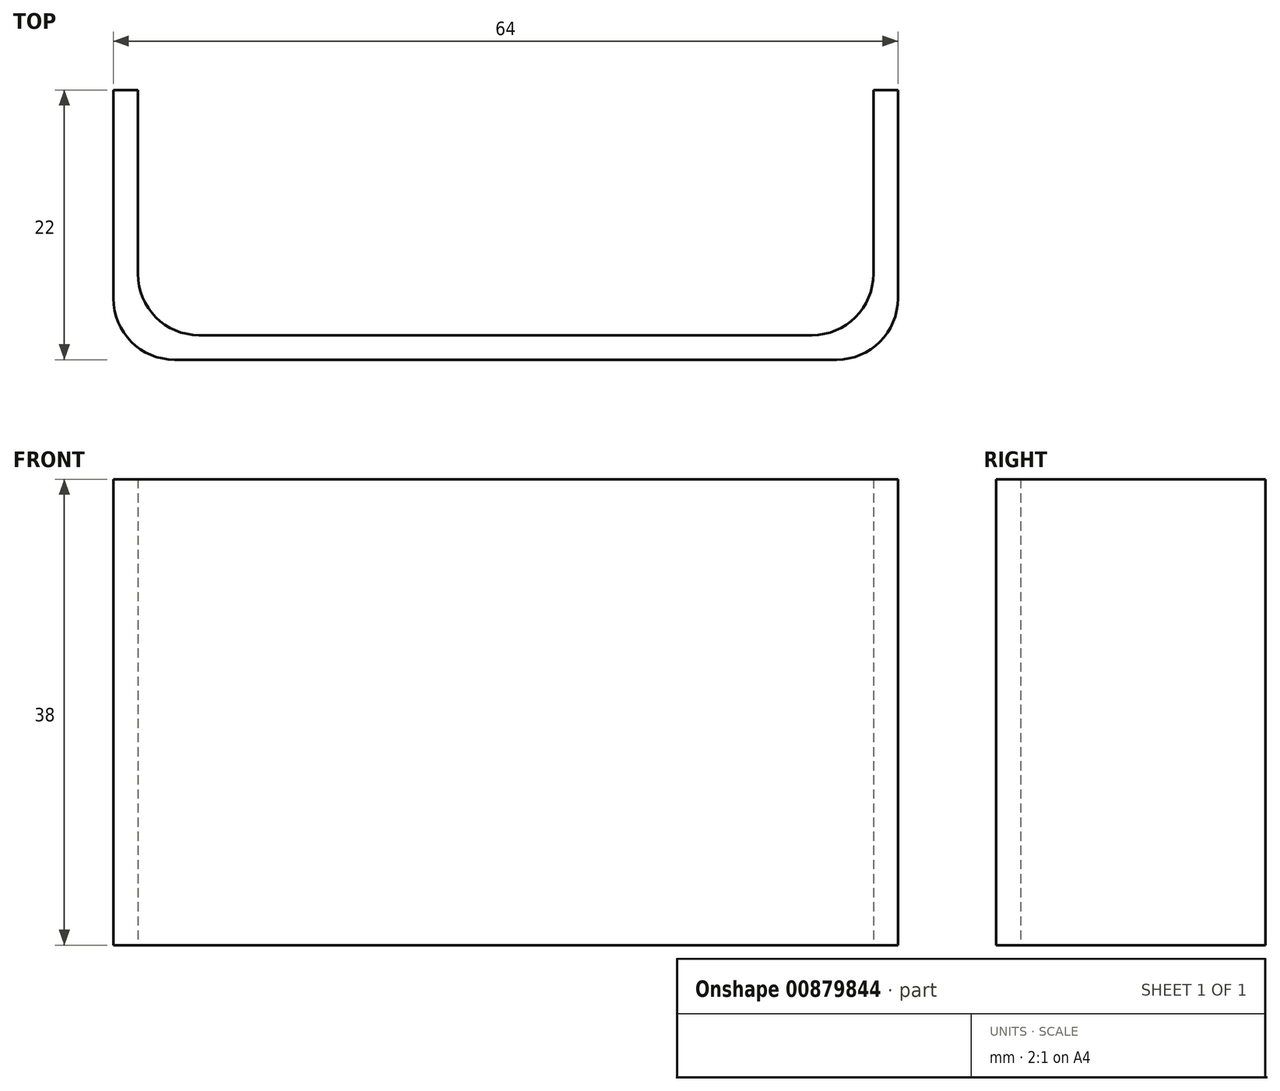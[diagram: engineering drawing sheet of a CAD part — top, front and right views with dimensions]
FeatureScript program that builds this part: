
annotation { "Feature Type Name" : "Feature", "Feature Type Description" : "" }
export const myFeature = defineFeature(function(context is Context, id is Id, definition is map)
    precondition{}
    {
        {
            var Q0;
            Q0=qCreatedBy(makeId("Top.planeOp"),FACE);
            var sketch = newSketch(context, id + "F0", { "sketchPlane" : qUnion([Q0])});
            skLineSegment(sketch, "E0", {"start": v(0, 0) * mm, "end": v(25, 0) * mm});
            skLineSegment(sketch, "E1", {"start": v(30, 5) * mm, "end": v(30, 20) * mm});
            skLineSegment(sketch, "E2", {"start": v(30, 20) * mm, "end": v(32, 20) * mm});
            skLineSegment(sketch, "E3", {"start": v(32, 20) * mm, "end": v(32, 3) * mm});
            skLineSegment(sketch, "E4", {"start": v(27, -2) * mm, "end": v(0, -2) * mm});
            skPoint(sketch, "E5.visualSharp", {"position": v(30, 0) * mm});
            skArc(sketch, "E5.filletArc", {"start": v(25, 0) * mm, "mid": v(28.54, 1.46) * mm, "end": v(30, 5) * mm});
            skPoint(sketch, "E6.visualSharp", {"position": v(32, -2) * mm});
            skArc(sketch, "E6.filletArc", {"start": v(27, -2) * mm, "mid": v(30.54, -0.54) * mm, "end": v(32, 3) * mm});
            skLineSegment(sketch, "E7.MirrorCS", {"start": v(-30, 20) * mm, "end": v(-32, 20) * mm});
            skArc(sketch, "E8.MirrorCS", {"start": v(-27, -2) * mm, "mid": v(-30.54, -0.54) * mm, "end": v(-32, 3) * mm});
            skArc(sketch, "E9.MirrorCS", {"start": v(-25, 0) * mm, "mid": v(-28.54, 1.46) * mm, "end": v(-30, 5) * mm});
            skPoint(sketch, "E10.MirrorP", {"position": v(-32, -2) * mm});
            skPoint(sketch, "E11.MirrorP", {"position": v(-30, 0) * mm});
            skLineSegment(sketch, "E12.MirrorCS", {"start": v(-30, 5) * mm, "end": v(-30, 20) * mm});
            skLineSegment(sketch, "E13.MirrorCS", {"start": v(-27, -2) * mm, "end": v(0, -2) * mm});
            skLineSegment(sketch, "E14.MirrorCS", {"start": v(-32, 20) * mm, "end": v(-32, 3) * mm});
            skLineSegment(sketch, "E15.MirrorCS", {"start": v(0, 0) * mm, "end": v(-25, 0) * mm});
            skSolve(sketch);
        }
        {
            var Q0;
            Q0 = qSketchRegion(id + "F0", true);
            extrude(context, id + "F1", {"entities" : qUnion([Q0]), "depth" : 38 * mm, "offsetDistance" : 25 * mm});
        }
    });
